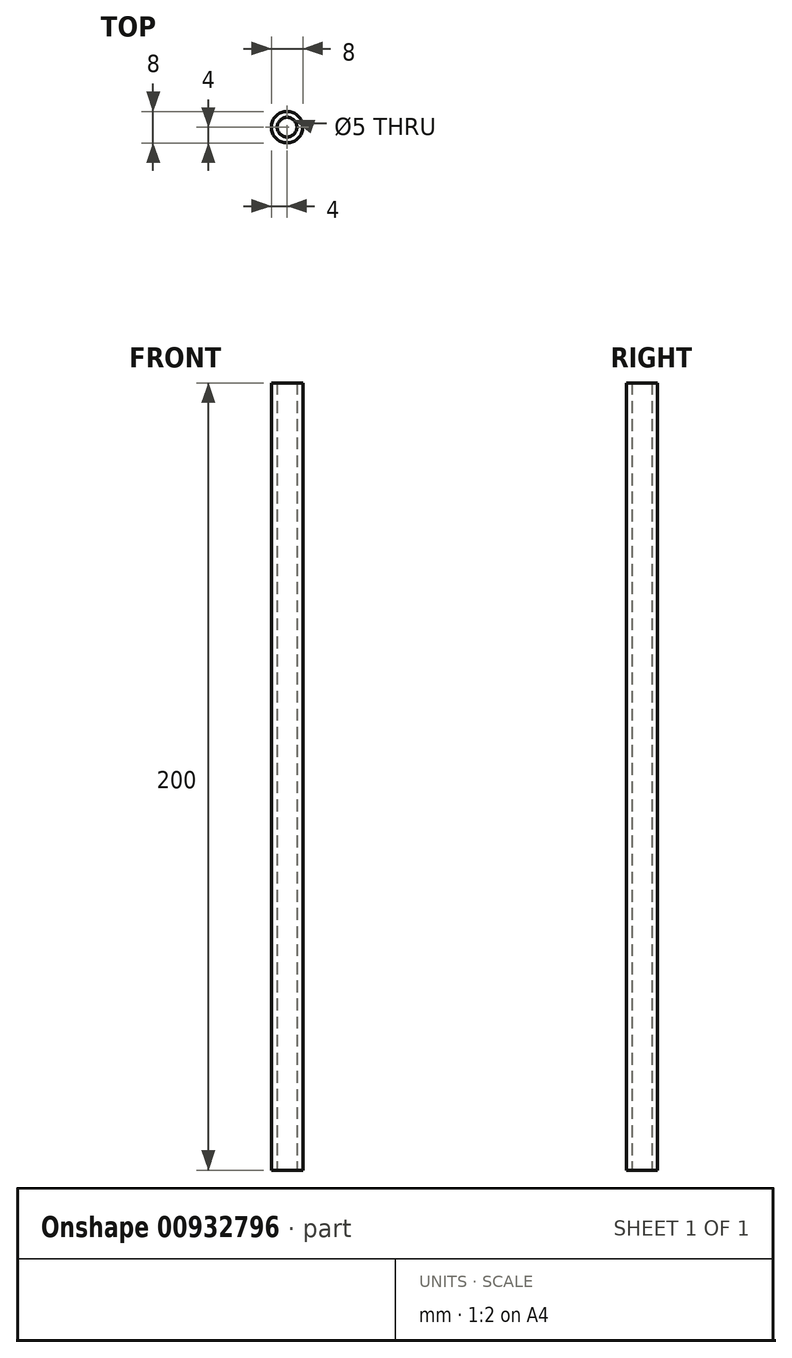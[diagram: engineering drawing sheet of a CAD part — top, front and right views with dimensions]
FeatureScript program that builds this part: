
annotation { "Feature Type Name" : "Feature", "Feature Type Description" : "" }
export const myFeature = defineFeature(function(context is Context, id is Id, definition is map)
    precondition{}
    {
        {
            var Q0;
            Q0=qCreatedBy(makeId("Top.planeOp"),FACE);
            var sketch = newSketch(context, id + "F0", { "sketchPlane" : qUnion([Q0])});
            skCircle(sketch, "E0", {"center": v(0, 0) * mm, "radius": 4 * mm});
            skCircle(sketch, "E1", {"center": v(0, 0) * mm, "radius": 2.5 * mm});
            skSolve(sketch);
        }
        {
            var Q0;
            Q0 = qSketchRegion(id + "F0", true);
            extrude(context, id + "F1", {"entities" : qUnion([Q0]), "depth" : 200 * mm, "offsetDistance" : 25 * mm});
        }
    });
